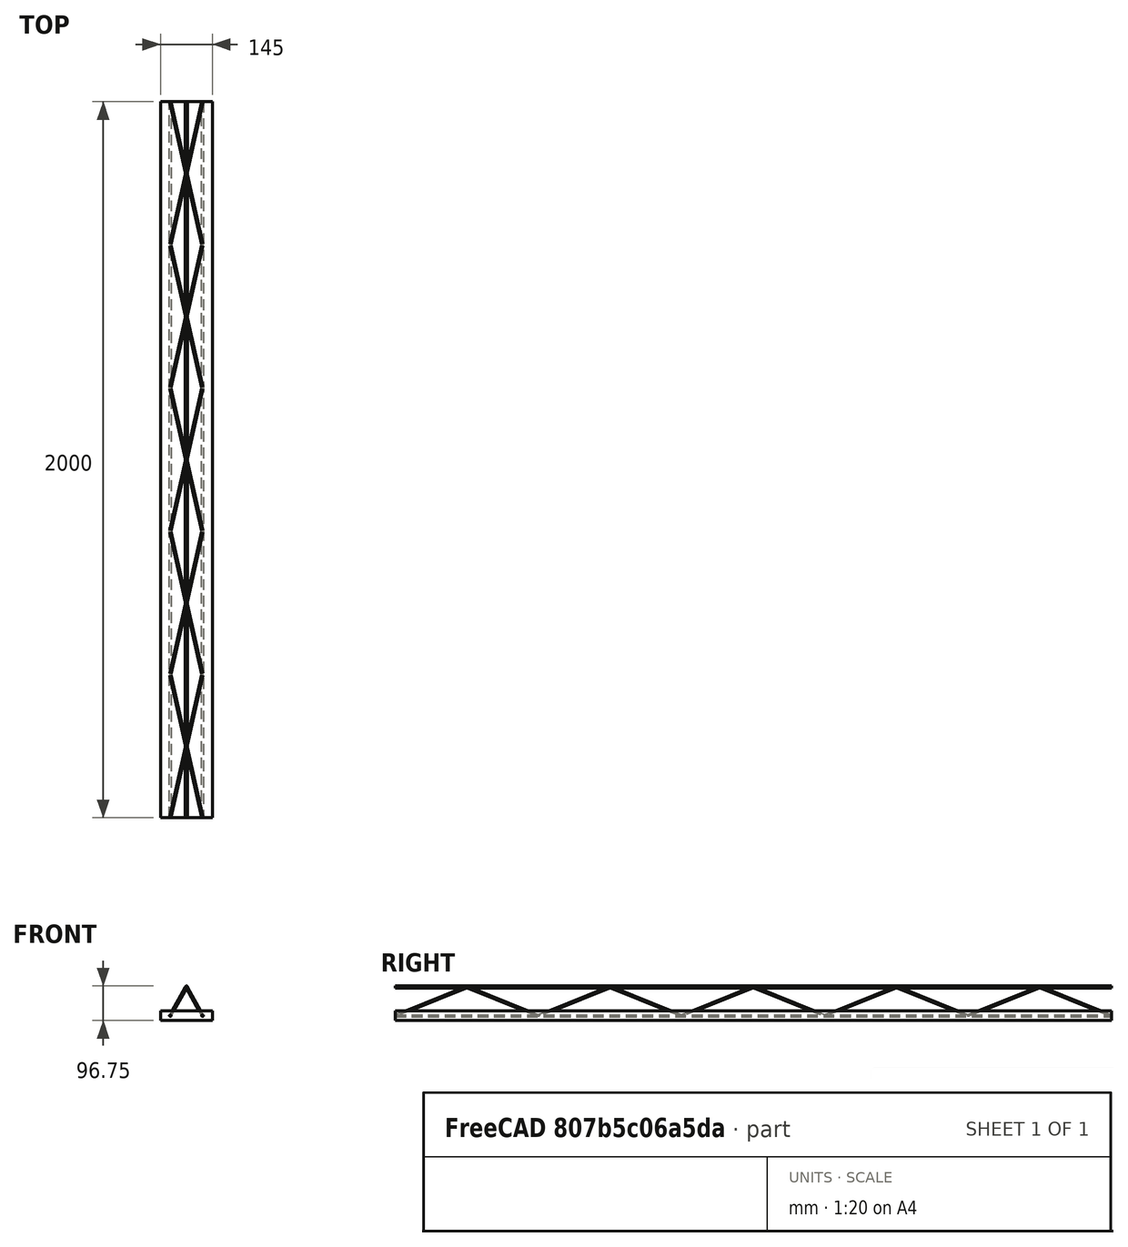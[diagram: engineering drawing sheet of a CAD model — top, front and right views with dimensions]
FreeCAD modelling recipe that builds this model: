
FCSTD DOCUMENT  (FreeCAD 1.0R38641 +468 (Git))
Label: VigaTreliçada_BIM_Parametrico
License: Creative Commons Attribution 3.0
LicenseURL: https://creativecommons.org/licenses/by/3.0/
objects: Sketcher::SketchObject×6, PartDesign::Pad×5, PartDesign::Body×5, Part::FeaturePython×4, PartDesign::Plane×3, Part::Compound×3, Spreadsheet::Sheet×2, PartDesign::Chamfer×1, PartDesign::Mirrored×1
note: 45 computed .brp shape members not serialized (recipe doc carries the construction recipe); baked Part::Feature solids carry a one-line shape summary decoded from their .brp

FEATURE [Sketcher::SketchObject] Sketch010  label="Trelica001"
  ArcFitTolerance = 1e-06
  AttachmentSupport = -> [XZ_Plane008]
  FullyConstrained = true
  MakeInternals = false
  MapMode = 5
  Placement = pos=(0,0,0) rot=(1,0,0;1.5708rad)
  expr: .Constraints.banzo_inf = <<Gerdau_Models>>.banzo_inf
  expr: Constraints[2] = <<Gerdau_Models>>.dist_banz_inf / 2
  sketch-geometry (1):
    g0: Circle CenterX=-45 CenterY=0 CenterZ=0 NormalX=0 NormalY=0 NormalZ=1 AngleXU=0 Radius=2.5
  constraints (3):
    c: Diameter(g0) = 5  'banzo_inf'
    c: PointOnObject(g0,g-1)
    c: DistanceX(g0,g-1) = 45
FEATURE [PartDesign::Pad] Pad008
  Direction = (0,-1,2e-16)
  Length = 2000
  Length2 = 10
  Placement = pos=(0,0,0) rot=(1,0,0;1.5708rad)
  Profile = -> Sketch010
  ReferenceAxis = -> Sketch010 [N_Axis]
  Refine = true
  Suppressed = false
  Type = 0
  expr: Length = <<Dimentions>>.comprimento
FEATURE [PartDesign::Body] Body008  label="Banzo_Inf_003"
  AllowCompound = false
  Group = -> [Sketch010,Pad008]
  Origin = -> Origin008
  Tip = -> Pad008
FEATURE [Sketcher::SketchObject] Sketch011
  ArcFitTolerance = 1e-06
  AttachmentSupport = -> [Sketch010]
  FullyConstrained = true
  MakeInternals = false
  MapMode = 2
  Placement = pos=(0,0,0) rot=(1,0,0;1.5708rad)
  expr: Constraints[0] = <<Gerdau_Models>>.banzo_inf
  expr: Constraints[2] = <<Gerdau_Models>>.dist_banz_inf / 2
  sketch-geometry (1):
    g0: Circle CenterX=45 CenterY=0 CenterZ=0 NormalX=0 NormalY=0 NormalZ=1 AngleXU=0 Radius=2.5
  constraints (3):
    c: Diameter(g0) = 5
    c: PointOnObject(g0,g-1)
    c: DistanceX(g-1,g0) = 45
FEATURE [PartDesign::Pad] Pad009
  Direction = (0,-1,2e-16)
  Length = 2000
  Length2 = 10
  Placement = pos=(0,0,0) rot=(1,0,0;1.5708rad)
  Profile = -> Sketch011
  ReferenceAxis = -> Sketch011 [N_Axis]
  Refine = true
  Suppressed = false
  Type = 0
  expr: Length = <<Dimentions>>.comprimento
FEATURE [PartDesign::Body] Body009  label="Banzo_Inf_004"
  AllowCompound = false
  Group = -> [Sketch011,Pad009]
  Origin = -> Origin009
  Tip = -> Pad009
FEATURE [Sketcher::SketchObject] Sketch012
  ArcFitTolerance = 1e-06
  AttachmentSupport = -> [Sketch010]
  FullyConstrained = true
  MakeInternals = false
  MapMode = 2
  Placement = pos=(0,0,0) rot=(1,0,0;1.5708rad)
  expr: Constraints[1] = <<Gerdau_Models>>.banzo_sup
  expr: Constraints[2] = <<Gerdau_Models>>.altura * 10
  sketch-geometry (1):
    g0: Circle CenterX=0 CenterY=80 CenterZ=0 NormalX=0 NormalY=0 NormalZ=1 AngleXU=0 Radius=3
  constraints (3):
    c: PointOnObject(g0,g-2)
    c: Diameter(g0) = 6
    c: DistanceY(g-1,g0) = 80
FEATURE [PartDesign::Pad] Pad010
  Direction = (0,-1,2e-16)
  Length = 2000
  Length2 = 10
  Placement = pos=(0,0,0) rot=(1,0,0;1.5708rad)
  Profile = -> Sketch012
  ReferenceAxis = -> Sketch012 [N_Axis]
  Refine = true
  Suppressed = false
  Type = 0
  expr: Length = <<Dimentions>>.comprimento
FEATURE [PartDesign::Plane] DatumPlane003
  AttachmentOffset = pos=(0,0,45) rot=(0,1,0;0.512389rad)
  AttachmentSupport = -> [Pad010]
  Length = 216.647
  MapMode = 4
  Placement = pos=(45,0,-1e-14) rot=(0.504846,0,0.863209;3.14159rad)
  ResizeMode = 0
  Width = 2123.02
  expr: .AttachmentOffset.Base.z = <<Gerdau_Models>>.dist_banz_inf / 2
  expr: .AttachmentOffset.Rotation.Pitch = atan(<<Gerdau_Models>>.dist_banz_inf / 2 / (<<Gerdau_Models>>.altura * 10))
FEATURE [PartDesign::Body] Body010  label="Banzo_sup001"
  AllowCompound = false
  Group = -> [Sketch012,Pad010,DatumPlane003]
  Origin = -> Origin010
  Tip = -> Pad010
FEATURE [Sketcher::SketchObject] Sketch013
  ArcFitTolerance = 1e-06
  AttachmentSupport = -> [DatumPlane003]
  ExternalGeometry = -> [Pad009,Pad010]
  FullyConstrained = true
  MakeInternals = false
  MapMode = 5
  Placement = pos=(45,0,-1.07e-14) rot=(0.504846,0,0.863209;3.14159rad)
  expr: Constraints[2] = <<Gerdau_Models>>.dist_diagonal
  expr: Constraints[9] = <<Gerdau_Models>>.dist_diagonal * 2
  sketch-geometry (3):
    g0: LineSegment StartX=8.9e-15 StartY=0 StartZ=0 EndX=91.7878 EndY=200 EndZ=0
    g1: LineSegment StartX=91.7878 StartY=-2.84e-14 StartZ=0 EndX=91.7878 EndY=200 EndZ=0
    g2: LineSegment StartX=1.07e-14 StartY=400 StartZ=0 EndX=91.7878 EndY=200 EndZ=0
  constraints (10):
    c: Symmetric(g-3,g-3,g0)
    c: Vertical(g1)
    c: DistanceY(g1,g1) = 200
    c: DistanceY(g0,g1) = 0
    c: DistanceX(g0,g1) = 0
    c: Symmetric(g-4,g-4,g1)
    c: DistanceX(g2,g0) = 0
    c: DistanceX(g2,g0) = 0
    c: DistanceY(g0,g2) = 0
    c: DistanceY(g-3,g2) = 400
FEATURE [PartDesign::Plane] DatumPlane004
  AttachmentSupport = -> [Sketch013]
  Length = 217.963
  MapMode = 7
  Placement = pos=(45,0,-2.7e-15) rot=(0.09136,0.822241,0.561758;3.01692rad)
  ResizeMode = 0
  Width = 227.355
FEATURE [PartDesign::Plane] DatumPlane005
  AttachmentSupport = -> [Sketch013]
  Length = 217.963
  MapMode = 7
  Placement = pos=(45,-400,-2.84e-14) rot=(0.991067,0.110119,0.075233;1.95121rad)
  ResizeMode = 0
  Width = 227.355
FEATURE [Sketcher::SketchObject] Sketch014
  ArcFitTolerance = 1e-06
  AttachmentSupport = -> [DatumPlane004]
  FullyConstrained = true
  MakeInternals = false
  MapMode = 5
  Placement = pos=(45,-1.8e-15,-3.1e-15) rot=(0.09136,0.822241,0.561758;3.01692rad)
  expr: Constraints[1] = <<Gerdau_Models>>.diagonal
  sketch-geometry (1):
    g0: Circle CenterX=0 CenterY=0 CenterZ=0 NormalX=0 NormalY=0 NormalZ=1 AngleXU=0 Radius=2.1
  constraints (2):
    c: Coincident(g0,g-1)
    c: Diameter(g0) = 4.2
FEATURE [PartDesign::Pad] Pad011
  Direction = (0.204493,0.908856,-0.363542)
  Length = 10
  Length2 = 10
  Placement = pos=(45,0,-2.7e-15) rot=(0.09136,0.822241,0.561758;3.01692rad)
  Profile = -> Sketch014
  ReferenceAxis = -> Sketch014 [N_Axis]
  Refine = true
  Suppressed = false
  Type = 3
  UpToFace = -> Pad010 [Face1]
FEATURE [PartDesign::Chamfer] Chamfer001
  Angle = 45
  Base = -> Pad011 [Face2]
  BaseFeature = -> Pad011
  ChamferType = 0
  FlipDirection = false
  Placement = pos=(45,0,-2.7e-15) rot=(0.09136,0.822241,0.561758;3.01692rad)
  Refine = true
  Size = 2.1
  Size2 = 1
  SupportTransform = false
  Suppressed = false
  UseAllEdges = false
  expr: Size = <<Gerdau_Models>>.diagonal / 2
FEATURE [PartDesign::Mirrored] Mirrored002
  BaseFeature = -> Chamfer001
  MirrorPlane = -> YZ_Plane011
  Placement = pos=(45,0,-2.7e-15) rot=(0.09136,0.822241,0.561758;3.01692rad)
  Refine = true
  Suppressed = false
  TransformMode = 1
FEATURE [PartDesign::Body] Body011  label="Diagonal_002"
  AllowCompound = false
  Group = -> [Sketch013,DatumPlane004,Sketch014,Pad011,Chamfer001,Mirrored002,DatumPlane005]
  Origin = -> Origin011
  Tip = -> Mirrored002
FEATURE [Part::Compound] Compound004  label="Compound005"
  Links = -> [Body011]
FEATURE [Part::FeaturePython] Array004  # Draft array (typed FeaturePython)
  AlwaysSyncPlacement = false
  Angle = 360
  ArrayType = 0
  Axis = (0,0,1)
  Base = -> Compound004
  Center = (0,0,0)
  Count = 5
  ExpandArray = false
  Fuse = false
  IntervalAxis = (0,0,0)
  IntervalX = (200,0,0)
  IntervalY = (0,-400,0)
  IntervalZ = (0,0,100)
  NumberCircles = 3
  NumberPolar = 5
  NumberX = 1
  NumberY = 5
  NumberZ = 1
  PlacementList = 5 placements: arithmetic series from (0,0,0) step (0,-400,0) to (0,-1600,0)
  RadialDistance = 50
  ScaleList = (5) [(1,1,1),(1,1,1),(1,1,1),(1,1,1),(1,1,1)]
  Symmetry = 1
  TangentialDistance = 25
  expr: .IntervalY.y = -<<Gerdau_Models>>.dist_diagonal * 2
  expr: NumberY = trunc((<<Dimentions>>.comprimento + <<Gerdau_Models>>.dist_diagonal) / (<<Gerdau_Models>>.dist_diagonal * 2))
FEATURE [Part::FeaturePython] Clone001  label="Compound003"  # Draft clone (typed FeaturePython)
  AttacherType = Attacher::AttachEngine3D
  Fuse = false
  Objects = -> [Compound004]
  Placement = pos=(0,-400,0) rot=(0,0,1;3.14159rad)
  Scale = (1,1,1)
  expr: .Placement.Base.y = -2 * <<Gerdau_Models>>.dist_diagonal
FEATURE [Part::FeaturePython] Array005  # Draft array (typed FeaturePython)
  AlwaysSyncPlacement = false
  Angle = 360
  ArrayType = 0
  Axis = (0,0,1)
  Base = -> Clone001
  Center = (0,0,0)
  Count = 5
  ExpandArray = false
  Fuse = false
  IntervalAxis = (0,0,0)
  IntervalX = (100,0,0)
  IntervalY = (0,-400,0)
  IntervalZ = (0,0,100)
  NumberCircles = 3
  NumberPolar = 5
  NumberX = 1
  NumberY = 5
  NumberZ = 1
  PlacementList = 5 placements: arithmetic series from (0,-400,0) step (0,-400,0) to (0,-2000,0)
  RadialDistance = 50
  ScaleList = (5) [(1,1,1),(1,1,1),(1,1,1),(1,1,1),(1,1,1)]
  Symmetry = 1
  TangentialDistance = 25
  expr: .IntervalY.y = -<<Gerdau_Models>>.dist_diagonal * 2
  expr: NumberY = trunc(<<Dimentions>>.comprimento / (<<Gerdau_Models>>.dist_diagonal * 2))
FEATURE [Sketcher::SketchObject] Sketch015
  ArcFitTolerance = 1e-06
  AttachmentSupport = -> [XY_Plane012]
  ExternalGeometry = -> [Pad009,Sketch010,Pad008]
  FullyConstrained = true
  MakeInternals = false
  MapMode = 5
  expr: Constraints[10] = <<Dimentions>>.cobrimento
  expr: Constraints[11] = <<Dimentions>>.cobrimento
  expr: Constraints[8] = <<Dimentions>>.comprimento
  sketch-geometry (4):
    g0: LineSegment StartX=-72.5 StartY=-2000 StartZ=0 EndX=-72.5 EndY=0 EndZ=0
    g1: LineSegment StartX=-72.5 StartY=0 StartZ=0 EndX=72.5 EndY=0 EndZ=0
    g2: LineSegment StartX=72.5 StartY=0 StartZ=0 EndX=72.5 EndY=-2000 EndZ=0
    g3: LineSegment StartX=72.5 StartY=-2000 StartZ=0 EndX=-72.5 EndY=-2000 EndZ=0
  constraints (12):
    c: Coincident(g0,g1)
    c: Coincident(g1,g2)
    c: Coincident(g2,g3)
    c: Coincident(g3,g0)
    c: Vertical(g0)
    c: Vertical(g2)
    c: Horizontal(g1)
    c: Horizontal(g3)
    c: DistanceY(g0,g0) = 2000
    c: DistanceY(g-4,g0) = 0
    c: DistanceX(g0,g-5) = 25
    c: DistanceX(g-6,g2) = 25
FEATURE [PartDesign::Pad] Pad012
  Direction = (0,0,1)
  Length = 27.5
  Length2 = 10
  Midplane = true
  Profile = -> Sketch015
  ReferenceAxis = -> Sketch015 [N_Axis]
  Refine = true
  Suppressed = false
  Type = 0
  expr: Length = <<Dimentions>>.cobrimento + <<Gerdau_Models>>.banzo_inf / 2
FEATURE [PartDesign::Body] Body012  label="Base002"
  AllowCompound = false
  Group = -> [Sketch015,Pad012]
  Origin = -> Origin012
  Tip = -> Pad012
FEATURE [Part::Compound] Compound003  label="Compound004"
  Links = -> [Body012,Body010,Body009,Body008,Array004,Array005]
FEATURE [Part::FeaturePython] Component003  label="Trelica_Gerdau_"  # Arch/BIM 119 (typed FeaturePython)
  Area = 290000
  Base = -> Compound003
  Description = Viga Trelicada
  HorizontalArea = 0
  IfcData = attributes={"GlobalId": {"name": "GlobalId", "type": "IfcGloballyUniqueId", "is_enum": false, "enum_values": []}, "Description": {"... (+480 chars omitted),+1 more (map truncated)
  IfcType = 119
  Length = 2000
  MoveBase = false
  MoveWithHost = false
  PerimeterLength = 0
  PredefinedType = 0
  VerticalArea = 0
  expr: Area = <<Dimentions>>.comprimento * (<<Gerdau_Models>>.dist_banz_inf + <<Gerdau_Models>>.banzo_inf + 2 * <<Dimentions>>.cobrimento)
  expr: Length = <<Dimentions>>.comprimento
FEATURE [Spreadsheet::Sheet] Spreadsheet005  label="Gerdau_Models"
  Design_Gerdau = 5
  cells = A1='Designação; B1='Peso (kg/m); C1='Altura (cm); D1='Banzo superior (mm); E1='Diagonal (mm); F1='Banzo inferior (mm); G1='Dist Banzo Inf (mm); H1='Dist Diagonal (mm); A2==hiddenref(Compound005.Design_Gerdau.String); B2==.B11; C2(altura)==.C11; D2(banzo_sup)==.D11; E2(diagonal)==.E11; F2(banzo_inf)==.F11; G2(dist_banz_inf)==.G11; H2(dist_diagonal)==.H11; A3='TR 12646; B3=1.016; C3=12; D3=6; E3=4.2; F3=6; G3=90; H3=400; A4='TR 16745; B4=1.032; C4=16; D4=7; E4=4.2; F4=5; G4=90; H4=200; A5='TR 16746; B5=1.168; C5=16; D5=7; E5=4.2; F5=6; G5=90; H5=200; A6='TR 20745; B6=1.111; C6=20; D6=7; E6=4.2; F6=5; G6=90; H6=200; A7='TR 20756; B7=1.446; C7=20; D7=7; E7=5; F7=6; G7=90; H7=200; A8='TR 25856; B8=1.686; C8=25; D8=8; E8=5; F8=6; G8=90; H8=200; A9='TR 25857; B9=1.855; C9=25; D9=8; E9=5; F9=7; G9=90; H9=200; A10='TR 08644; B10=0.735; C10=8; D10=6; E10=4.2; F10=4.2; G10=90; H10=200; A11='TR 08645; B11=0.821; C11=8; D11=6; E11=4.2; F11=5; G11=90; H11=200
  expr: .Design_Gerdau.Enum = cells[<<A3:|>>]
  expr: .cells.Bind.B2.ZZ2 = tuple(.cells; <<B>> + str(hiddenref(Compound005.Design_Gerdau) + 3); <<ZZ>> + str(hiddenref(Compound005.Design_Gerdau) + 3))
FEATURE [Spreadsheet::Sheet] Spreadsheet006  label="Dimentions"
  cells = A1='Comprimento (mm); B1='Cobrimento (mm); A2(comprimento)=2000; B2(cobrimento)=25
FEATURE [Part::Compound] Compound005  label="Trelica_Gerdau"
  Area = 290000
  Design_Gerdau = 8
  Length = 200
  Links = -> [Component003,Spreadsheet005,Spreadsheet006]
  expr: .Design_Gerdau.Enum = Spreadsheet005.cells[<<A3:|>>]
  expr: Area = <<Dimentions>>.comprimento * (<<Gerdau_Models>>.dist_banz_inf + <<Gerdau_Models>>.banzo_inf + 2 * <<Dimentions>>.cobrimento)
  expr: Length = 200 mm
